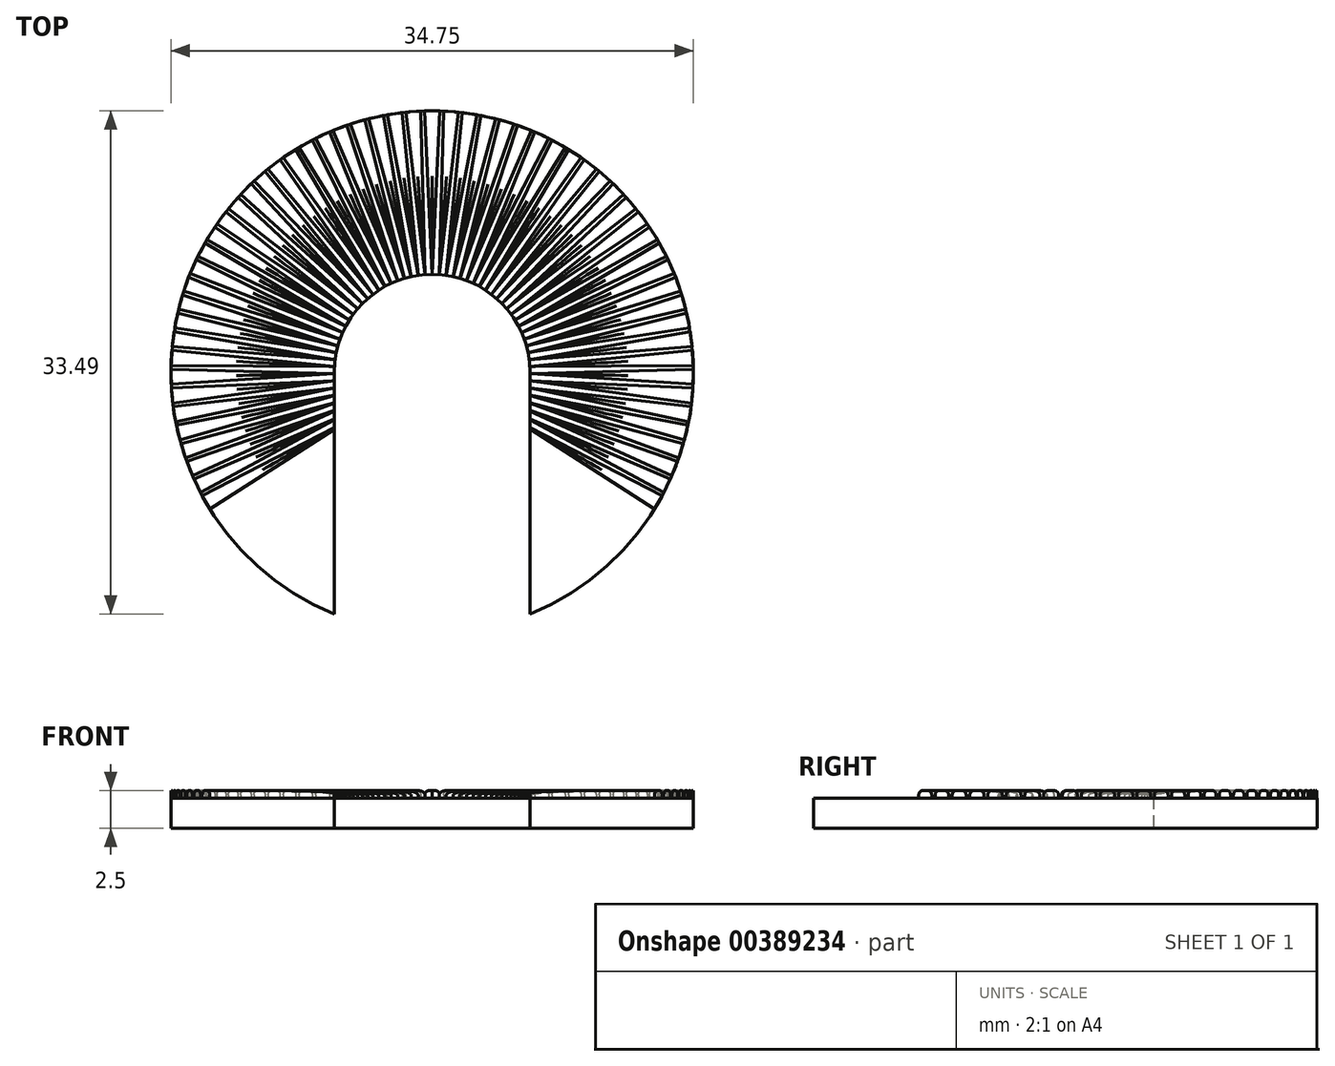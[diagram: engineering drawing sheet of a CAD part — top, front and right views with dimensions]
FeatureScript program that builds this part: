
annotation { "Feature Type Name" : "Feature", "Feature Type Description" : "" }
export const myFeature = defineFeature(function(context is Context, id is Id, definition is map)
    precondition{}
    {
        {
            var Q0;
            Q0=qCreatedBy(makeId("Top.planeOp"),FACE);
            var sketch = newSketch(context, id + "F0", { "sketchPlane" : qUnion([Q0])});
            skArc(sketch, "E0", {"start": v(6.5, -16.11) * mm, "mid": v(0, 17.38) * mm, "end": v(-6.5, -16.11) * mm});
            skArc(sketch, "E1", {"start": v(6.5, 0) * mm, "mid": v(0, 6.5) * mm, "end": v(-6.5, 0) * mm});
            skLineSegment(sketch, "E2", {"start": v(-6.5, 0) * mm, "end": v(-6.5, -16.11) * mm});
            skLineSegment(sketch, "E3", {"start": v(6.5, 0) * mm, "end": v(6.5, -16.11) * mm});
            skCircle(sketch, "E4", {"center": v(-11.94, 0) * mm, "radius": 2.5 * mm});
            skCircle(sketch, "E5.1.0.0", {"center": v(11.94, 0) * mm, "radius": 2.5 * mm});
            skLineSegment(sketch, "E5.direction1", {"start": v(-11.94, 0) * mm, "end": v(11.94, 0) * mm, "construction": true});
            skSolve(sketch);
        }
        {
            var Q0;
            Q0=makeQuery(id+"F0.imprint","IMPRINT",FACE,{"disambiguationData":[TD([[makeQuery(id+"F0.imprint","IMPRINT",EDGE,{"derivedFrom":sQuery(id+"F0.wireOp",EDGE,"E4")}),1.0]])]});
            var Q1;
            Q1=makeQuery(id+"F0.imprint","IMPRINT",FACE,{"disambiguationData":[TD([[makeQuery(id+"F0.imprint","IMPRINT",EDGE,{"derivedFrom":sQuery(id+"F0.wireOp",EDGE,"E5.1.0.0")}),1.0]])]});
            extrude(context, id + "F1", {"entities" : qUnion([Q0, Q1]), "depth" : 1 * mm});
        }
        {
            var Q0;
            Q0=qSketchRegion(id+"F0",true);
            var Q1;
            Q1=makeQuery(id+"F0.imprint","IMPRINT",FACE,{"disambiguationData":[TD([[makeQuery(id+"F0.imprint","IMPRINT",EDGE,{"derivedFrom":sQuery(id+"F0.wireOp",EDGE,"E4")}),1.0]])]});
            var Q2;
            Q2=makeQuery(id+"F0.imprint","IMPRINT",FACE,{"disambiguationData":[TD([[makeQuery(id+"F0.imprint","IMPRINT",EDGE,{"derivedFrom":sQuery(id+"F0.wireOp",EDGE,"E5.1.0.0")}),1.0]])]});
            extrude(context, id + "F2", {"entities" : qUnion([Q0, Q1, Q2]), "operationType" : NewBodyOperationType.ADD, "depth" : 2 * mm});
        }
        {
            var Q0;
            Q0=makeQuery(id+"F2.opExtrude","CAP_FACE",FACE,{"disambiguationData":[OSD([sQuery(id+"F0.wireOp",EDGE,"E0"),sQuery(id+"F0.wireOp",EDGE,"E1"),sQuery(id+"F0.wireOp",EDGE,"E2"),sQuery(id+"F0.wireOp",EDGE,"E3")])],"isStart":false});
            var sketch = newSketch(context, id + "F3", { "sketchPlane" : qUnion([Q0])});
            skLineSegment(sketch, "E6", {"start": v(0, 6.5) * mm, "end": v(-0.5, 17.37) * mm});
            skLineSegment(sketch, "E7", {"start": v(-0.5, 17.37) * mm, "end": v(0.5, 17.37) * mm});
            skLineSegment(sketch, "E8", {"start": v(0.5, 17.37) * mm, "end": v(0, 6.5) * mm});
            skSolve(sketch);
        }
        {
            var Q0;
            Q0=makeQuery(id+"F3.imprint","IMPRINT",FACE,{"disambiguationData":[TD([[makeQuery(id+"F3.imprint","IMPRINT",EDGE,{"derivedFrom":sQuery(id+"F3.wireOp",EDGE,"E6")}),-1.0]])]});
            extrude(context, id + "F4", {"entities" : qUnion([Q0]), "depth" : 0.5 * mm});
        }
        {
            var Q0;
            Q0=makeQuery(id+"F4.opExtrude","CAP_EDGE",EDGE,{"disambiguationData":[OSD([sQuery(id+"F3.wireOp",EDGE,"E8")])],"isStart":false});
            var Q1;
            Q1=makeQuery(id+"F4.opExtrude","CAP_EDGE",EDGE,{"disambiguationData":[OSD([sQuery(id+"F3.wireOp",EDGE,"E6")])],"isStart":false});
            fillet(context, id + "F5", {"entities" : qUnion([Q0, Q1]), "radius" : 0.3 * mm, "tangentPropagation" : true, "allowEdgeOverflow" : false});
        }
        {
            var Q0;
            Q0=qCreatedBy(makeId("Right.planeOp"),FACE);
            var sketch = newSketch(context, id + "F6", { "sketchPlane" : qUnion([Q0])});
            skLineSegment(sketch, "E9", {"start": v(0, -30.46) * mm, "end": v(0, 45.43) * mm, "construction": true});
            skSolve(sketch);
        }
        {
            var Q0;
            Q0=makeQuery(id+"F4.opExtrude","SWEPT_BODY",BODY,{"disambiguationData":[OSD([sQuery(id+"F3.wireOp",EDGE,"E6"),sQuery(id+"F3.wireOp",EDGE,"E7"),sQuery(id+"F3.wireOp",EDGE,"E8")])]});
            var Q1;
            Q1=sQuery(id+"F6.wireOp",EDGE,"E9");
            circularPattern(context, id + "F7", {"entities" : qUnion([Q0]), "axis" : qUnion([Q1]), "angle" : 120 * degree, "instanceCount" : 30, "oppositeDirection" : true, "equalSpace" : true});
        }
        {
            var Q0;
            Q0=makeQuery(id+"F4.opExtrude","SWEPT_BODY",BODY,{"disambiguationData":[OSD([sQuery(id+"F3.wireOp",EDGE,"E6"),sQuery(id+"F3.wireOp",EDGE,"E7"),sQuery(id+"F3.wireOp",EDGE,"E8")])]});
            var Q1;
            Q1=sQuery(id+"F6.wireOp",EDGE,"E9");
            circularPattern(context, id + "F8", {"entities" : qUnion([Q0]), "axis" : qUnion([Q1]), "angle" : 120 * degree, "instanceCount" : 30, "equalSpace" : true});
        }
        {
            var Q0;
            Q0=qCreatedBy(makeId("Top.planeOp"),FACE);
            var sketch = newSketch(context, id + "F9", { "sketchPlane" : qUnion([Q0])});
            skLineSegment(sketch, "E10.bottom", {"start": v(-6.5, 0) * mm, "end": v(6.5, 0) * mm});
            skLineSegment(sketch, "E10.top", {"start": v(-6.5, -7.87) * mm, "end": v(6.5, -7.87) * mm});
            skLineSegment(sketch, "E10.left", {"start": v(-6.5, 0) * mm, "end": v(-6.5, -7.87) * mm});
            skLineSegment(sketch, "E10.right", {"start": v(6.5, 0) * mm, "end": v(6.5, -7.87) * mm});
            skSolve(sketch);
        }
        {
            var Q0;
            Q0=qSketchRegion(id+"F9",true);
            extrude(context, id + "F10", {"entities" : qUnion([Q0]), "operationType" : NewBodyOperationType.REMOVE, "depth" : 25 * mm});
        }
    });
